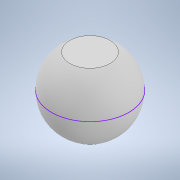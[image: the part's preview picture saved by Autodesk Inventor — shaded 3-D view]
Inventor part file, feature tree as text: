
AUTODESK INVENTOR PART (.ipt)
format: ipt  version: 2022 (Build 260153000, 153)  size: 126,976 bytes
history: native  units: in
note: dims shown in document units (in); Inventor stores cm internally (conversion verified against a paired STEP export)
features: sketch x2, revolve x1
ambient origin geometry x8: Origin, YZ Plane, XZ Plane, XY Plane, X Axis, Y Axis, Z Axis, Center Point
bodies: Body1 (feature_tree)
feature tree (3):
  revolve  "Revolution2"  Angle=90.0deg
  sketch  "Sketch4"
  sketch  "Sketch3"  dims[d3=2.5in d6=90.0deg]
